# Revit family: TRIBUTARY 18 X 54
name_source: partatom
category: Generic Models
units: mm (PartAtom-declared; Revit-internal decimal feet)

## family parameters
Can host rebar = No
Cut with Voids When Loaded = No
Host = Face
Maintain Annotation Orientation = No
Part Type = Normal
Room Calculation Point = No
Round Connector Dimension = Use Diameter
Shared = No

## types (5) — shared parameters
1/2 STICK = 2' - 3"
Default Elevation = 4' - 0"
PANEL LENGTH = 4' - 6"
PANEL MATERIAL = WF - PLYWOOD
PANEL WIDTH = 1' - 6"
STICKS PER WIDTH = 3

## per-type parameters (varying)
| type | DARK CLADDING MATERIAL | LIGHT CLADDING MATERIAL |
| TRIBUTARY - 18 X 54 - ELWAH | WF - TRIBUTARY - ELWAH - DARK | WF - TRIBUTARY - ELWAH - LIGHT |
| TRIBUTARY - 18 X 54 - HAMMA HAMMA | WF - TRIBUTARY - HAMMA HAMMA - DARK | WF - TRIBUTARY - HAMMA HAMMA - LIGHT |
| TRIBUTARY - 18 X 54 - NISQUALLY | WF - TRIBUTARY - NISQUALLY - DARK | WF - TRIBUTARY - NISQUALLY - LIGHT |
| TRIBUTARY - 18 X 54 - SKAGIT | WF - TRIBUTARY - SKAGIT - DARK | WF - TRIBUTARY -SKAGIT - LIGHT |
| TRIBUTARY - 18 X 54 - WILLAPA | WF - TRIBUTARY - WILLAPA - DARK | WF - TRIBUTARY - WILLAPA - LIGHT |

## geometry (parser evidence)
native form markers: Sweep x5
no freeform markers — native parametric forms only
